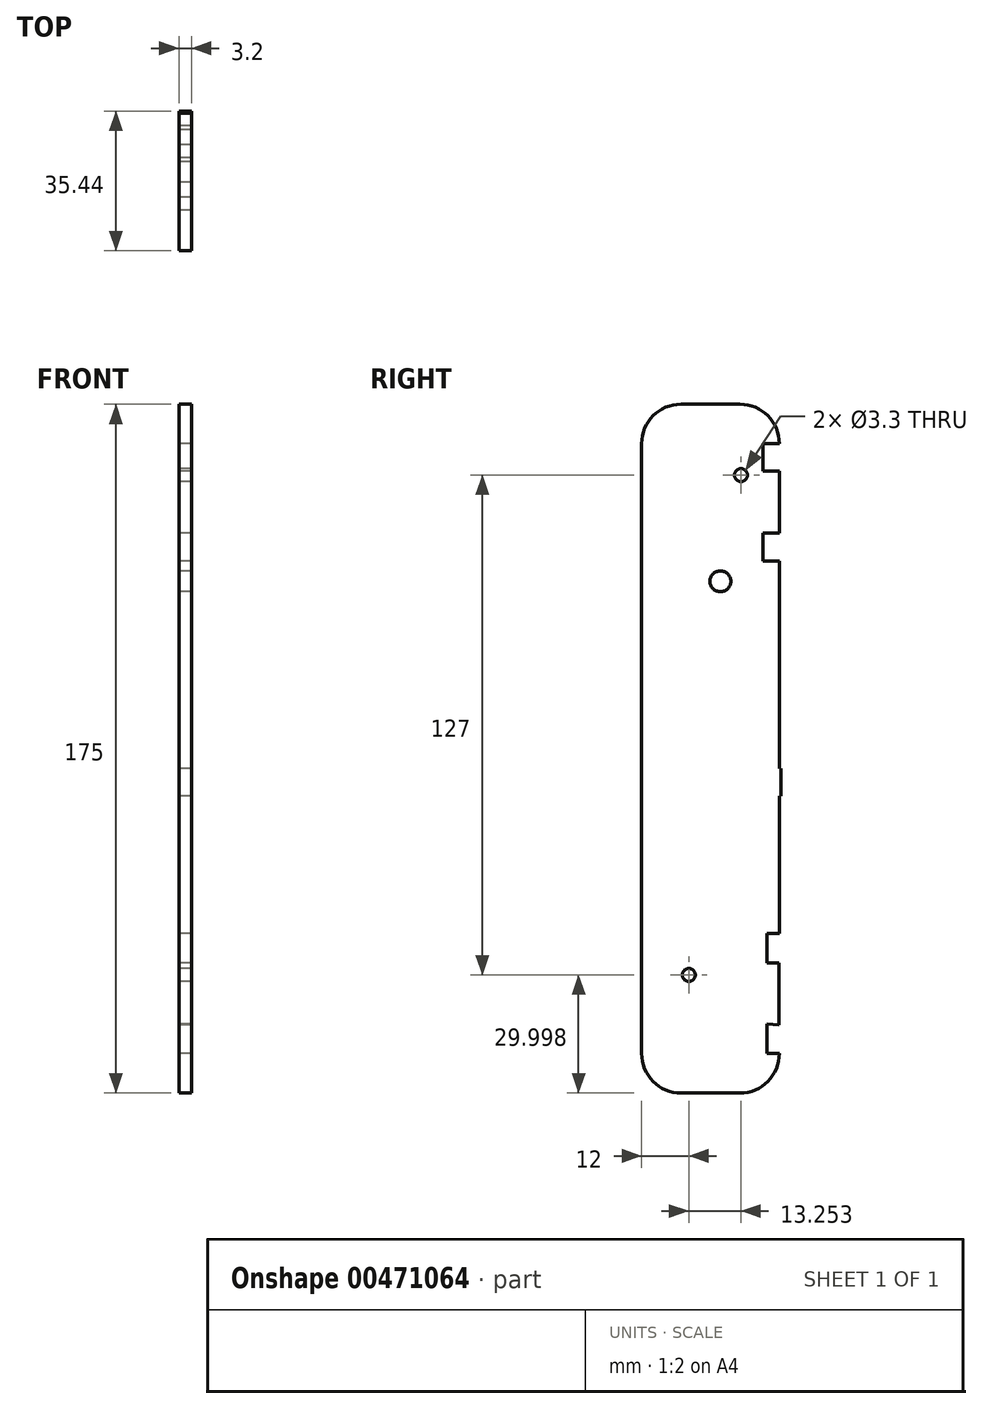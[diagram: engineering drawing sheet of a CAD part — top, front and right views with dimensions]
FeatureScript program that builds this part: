
annotation { "Feature Type Name" : "Feature", "Feature Type Description" : "" }
export const myFeature = defineFeature(function(context is Context, id is Id, definition is map)
    precondition{}
    {
        {
            var Q0;
            Q0=qCreatedBy(makeId("Right.planeOp"),FACE);
            var sketch = newSketch(context, id + "F0", { "sketchPlane" : qUnion([Q0])});
            skLineSegment(sketch, "E0.bottom", {"start": v(-7.66, 138.7) * mm, "end": v(7.34, 138.7) * mm});
            skLineSegment(sketch, "E0.top", {"start": v(-7.66, -36.3) * mm, "end": v(7.34, -36.3) * mm});
            skLineSegment(sketch, "E0.left", {"start": v(-17.66, 61.95) * mm, "end": v(-17.66, -19.05) * mm});
            skLineSegment(sketch, "E0.right", {"start": v(17.34, 121.7) * mm, "end": v(17.34, 118.42) * mm});
            skPoint(sketch, "E1.visualSharp", {"position": v(-17.66, 138.7) * mm});
            skArc(sketch, "E1.filletArc", {"start": v(-7.66, 138.7) * mm, "mid": v(-14.73, 135.78) * mm, "end": v(-17.66, 128.7) * mm});
            skPoint(sketch, "E2.visualSharp", {"position": v(17.34, 138.7) * mm});
            skArc(sketch, "E2.filletArc", {"start": v(17.34, 128.7) * mm, "mid": v(14.41, 135.78) * mm, "end": v(7.34, 138.7) * mm});
            skPoint(sketch, "E3.visualSharp", {"position": v(17.34, -36.3) * mm});
            skArc(sketch, "E3.filletArc", {"start": v(7.34, -36.3) * mm, "mid": v(14.41, -33.36) * mm, "end": v(17.34, -26.3) * mm});
            skPoint(sketch, "E4.visualSharp", {"position": v(-17.66, -36.3) * mm});
            skArc(sketch, "E4.filletArc", {"start": v(-17.66, -26.3) * mm, "mid": v(-14.73, -33.36) * mm, "end": v(-7.66, -36.3) * mm});
            skCircle(sketch, "E5", {"center": v(2.34, 93.7) * mm, "radius": 2.65 * mm});
            skCircle(sketch, "E6", {"center": v(-5.66, -6.3) * mm, "radius": 1.65 * mm});
            skCircle(sketch, "E7", {"center": v(7.6, 120.7) * mm, "radius": 1.65 * mm});
            skLineSegment(sketch, "E8", {"start": v(17.34, 128.7) * mm, "end": v(13.14, 128.7) * mm});
            skLineSegment(sketch, "E9", {"start": v(13.14, 128.7) * mm, "end": v(13.14, 121.7) * mm});
            skLineSegment(sketch, "E10", {"start": v(13.14, 121.7) * mm, "end": v(17.34, 121.7) * mm});
            skLineSegment(sketch, "E11", {"start": v(17.34, -26.3) * mm, "end": v(14.14, -26.3) * mm});
            skLineSegment(sketch, "E12", {"start": v(14.14, -26.3) * mm, "end": v(14.14, -18.8) * mm});
            skLineSegment(sketch, "E13.trimOffspring", {"start": v(17.34, 10.95) * mm, "end": v(17.34, 4.25) * mm});
            skLineSegment(sketch, "E14", {"start": v(-17.66, -19.05) * mm, "end": v(-17.66, -26.3) * mm});
            skLineSegment(sketch, "E15", {"start": v(-17.66, 128.7) * mm, "end": v(-17.66, 61.95) * mm});
            skLineSegment(sketch, "E16", {"start": v(17.34, 46.15) * mm, "end": v(17.78, 46.15) * mm});
            skLineSegment(sketch, "E17", {"start": v(17.78, 46.15) * mm, "end": v(17.78, 39.15) * mm});
            skLineSegment(sketch, "E18", {"start": v(17.34, 39.15) * mm, "end": v(17.78, 39.15) * mm});
            skLineSegment(sketch, "E19.trimOffspring", {"start": v(17.34, 39.15) * mm, "end": v(17.34, 17.95) * mm});
            skLineSegment(sketch, "E20", {"start": v(14.14, -3.25) * mm, "end": v(14.14, 4.25) * mm});
            skLineSegment(sketch, "E21", {"start": v(14.14, 4.25) * mm, "end": v(17.34, 4.25) * mm});
            skLineSegment(sketch, "E22", {"start": v(17.34, 17.95) * mm, "end": v(17.34, 10.95) * mm});
            skLineSegment(sketch, "E23.trimOffspring", {"start": v(17.34, 74.05) * mm, "end": v(17.34, 46.15) * mm});
            skLineSegment(sketch, "E24", {"start": v(17.24, -3.25) * mm, "end": v(17.24, -19.05) * mm});
            skLineSegment(sketch, "E25", {"start": v(14.14, -3.25) * mm, "end": v(17.24, -3.25) * mm});
            skLineSegment(sketch, "E26", {"start": v(14.14, -18.8) * mm, "end": v(17.24, -19.05) * mm});
            skLineSegment(sketch, "E27", {"start": v(17.34, 105.9) * mm, "end": v(13.14, 105.9) * mm});
            skLineSegment(sketch, "E28", {"start": v(13.14, 105.9) * mm, "end": v(13.14, 98.9) * mm});
            skLineSegment(sketch, "E29", {"start": v(13.14, 98.9) * mm, "end": v(17.34, 98.9) * mm});
            skLineSegment(sketch, "E30.trimOffspring", {"start": v(17.34, 98.9) * mm, "end": v(17.34, 81.05) * mm});
            skLineSegment(sketch, "E31", {"start": v(17.34, 81.05) * mm, "end": v(17.34, 74.05) * mm});
            skLineSegment(sketch, "E32.trimOffspring", {"start": v(17.34, 108.12) * mm, "end": v(17.34, 105.9) * mm});
            skLineSegment(sketch, "E33", {"start": v(17.34, 118.42) * mm, "end": v(17.34, 108.12) * mm});
            skSolve(sketch);
        }
        {
            var Q0;
            Q0 = qSketchRegion(id + "F0", true);
            extrude(context, id + "F1", {"entities" : qUnion([Q0]), "depth" : 3.2 * mm, "offsetDistance" : 25 * mm});
        }
    });
